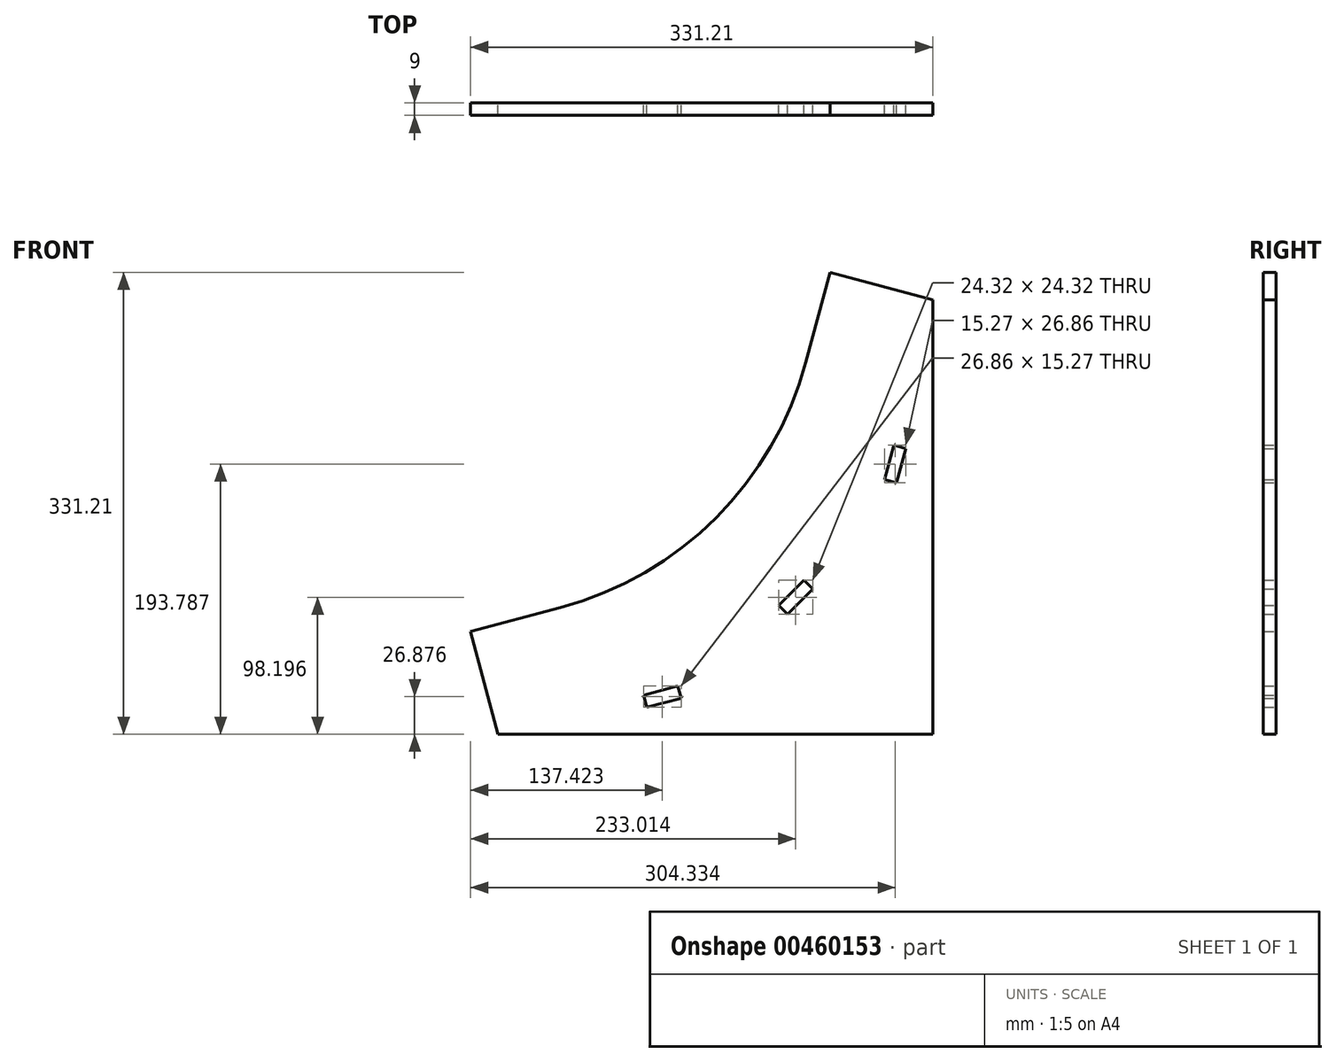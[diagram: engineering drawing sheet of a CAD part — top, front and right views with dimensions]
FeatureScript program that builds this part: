
annotation { "Feature Type Name" : "Feature", "Feature Type Description" : "" }
export const myFeature = defineFeature(function(context is Context, id is Id, definition is map)
    precondition{}
    {
        {
            var Q0;
            Q0=qCreatedBy(makeId("Front.planeOp"),FACE);
            var sketch = newSketch(context, id + "F0", { "sketchPlane" : qUnion([Q0])});
            skCircle(sketch, "E0", {"center": v(-175.95, 175.95) * mm, "radius": 248.83 * mm, "construction": true});
            skLineSegment(sketch, "E1", {"start": v(-175.95, -81.66) * mm, "end": v(-47.15, -47.15) * mm});
            skLineSegment(sketch, "E2", {"start": v(-47.15, -47.15) * mm, "end": v(47.15, 47.15) * mm});
            skLineSegment(sketch, "E3", {"start": v(47.15, 47.15) * mm, "end": v(81.66, 175.95) * mm});
            skPoint(sketch, "E4", {"position": v(0, 0) * mm});
            skLineSegment(sketch, "E5", {"start": v(-175.95, 175.95) * mm, "end": v(0, 0) * mm, "construction": true});
            skPoint(sketch, "E6", {"position": v(-111.55, -64.4) * mm});
            skPoint(sketch, "E7", {"position": v(64.4, 111.55) * mm});
            skLineSegment(sketch, "E8", {"start": v(-175.95, -81.66) * mm, "end": v(-156.23, -155.26) * mm});
            skLineSegment(sketch, "E9", {"start": v(-156.23, -155.26) * mm, "end": v(-27.42, -120.75) * mm});
            skLineSegment(sketch, "E10", {"start": v(-27.42, -120.75) * mm, "end": v(-47.15, -47.15) * mm});
            skLineSegment(sketch, "E11", {"start": v(-47.15, -47.15) * mm, "end": v(6.74, -101.03) * mm});
            skLineSegment(sketch, "E12", {"start": v(6.74, -101.03) * mm, "end": v(101.03, -6.74) * mm});
            skLineSegment(sketch, "E13", {"start": v(101.03, -6.74) * mm, "end": v(47.15, 47.15) * mm});
            skLineSegment(sketch, "E14", {"start": v(47.15, 47.15) * mm, "end": v(120.75, 27.42) * mm});
            skLineSegment(sketch, "E15", {"start": v(120.75, 27.42) * mm, "end": v(155.26, 156.23) * mm});
            skLineSegment(sketch, "E16", {"start": v(155.26, 156.23) * mm, "end": v(81.66, 175.95) * mm});
            skSolve(sketch);
        }
        {
            var Q0;
            Q0=qCreatedBy(makeId("Front.planeOp"),FACE);
            var sketch = newSketch(context, id + "F1", { "sketchPlane" : qUnion([Q0])});
            skLineSegment(sketch, "E17", {"start": v(-175.95, -81.66) * mm, "end": v(-156.23, -155.26) * mm});
            skLineSegment(sketch, "E18", {"start": v(-156.23, -155.26) * mm, "end": v(155.26, -155.26) * mm});
            skLineSegment(sketch, "E19", {"start": v(155.26, 156.23) * mm, "end": v(81.66, 175.95) * mm});
            skLineSegment(sketch, "E20", {"start": v(-175.95, -81.66) * mm, "end": v(-111.55, -64.4) * mm});
            skLineSegment(sketch, "E21", {"start": v(81.66, 175.95) * mm, "end": v(64.4, 111.55) * mm});
            skArc(sketch, "E22", {"start": v(-111.55, -64.4) * mm, "mid": v(0, 0) * mm, "end": v(64.4, 111.55) * mm});
            skLineSegment(sketch, "E23", {"start": v(155.26, 156.23) * mm, "end": v(155.26, -155.26) * mm});
            skLineSegment(sketch, "E24.bottom", {"start": v(-51.96, -127.32) * mm, "end": v(-27.42, -120.75) * mm});
            skLineSegment(sketch, "E24.top", {"start": v(-49.63, -136.02) * mm, "end": v(-25.1, -129.44) * mm});
            skLineSegment(sketch, "E24.left", {"start": v(-27.42, -120.75) * mm, "end": v(-25.1, -129.44) * mm});
            skLineSegment(sketch, "E24.right", {"start": v(-51.96, -127.32) * mm, "end": v(-49.63, -136.02) * mm});
            skLineSegment(sketch, "E25.bottom", {"start": v(44.9, -62.86) * mm, "end": v(62.86, -44.9) * mm});
            skLineSegment(sketch, "E25.top", {"start": v(51.27, -69.23) * mm, "end": v(69.23, -51.27) * mm});
            skLineSegment(sketch, "E25.left", {"start": v(44.9, -62.86) * mm, "end": v(51.27, -69.23) * mm});
            skLineSegment(sketch, "E25.right", {"start": v(62.86, -44.9) * mm, "end": v(69.23, -51.27) * mm});
            skLineSegment(sketch, "E26.bottom", {"start": v(120.75, 27.42) * mm, "end": v(127.32, 51.96) * mm});
            skLineSegment(sketch, "E26.top", {"start": v(129.44, 25.1) * mm, "end": v(136.02, 49.63) * mm});
            skLineSegment(sketch, "E26.left", {"start": v(120.75, 27.42) * mm, "end": v(129.44, 25.1) * mm});
            skLineSegment(sketch, "E26.right", {"start": v(127.32, 51.96) * mm, "end": v(136.02, 49.63) * mm});
            skPoint(sketch, "E27", {"position": v(-91.83, -138) * mm});
            skPoint(sketch, "E28", {"position": v(53.88, -53.88) * mm});
            skSolve(sketch);
        }
        {
            var Q0;
            Q0=makeQuery(id+"F1.imprint","IMPRINT",FACE,{"disambiguationData":[TD([[makeQuery(id+"F1.imprint","IMPRINT",EDGE,{"derivedFrom":sQuery(id+"F1.wireOp",EDGE,"E17")}),1.0]])]});
            extrude(context, id + "F2", {"entities" : qUnion([Q0]), "endBound" : BoundingType.SYMMETRIC, "depth" : 9 * mm});
        }
    });
